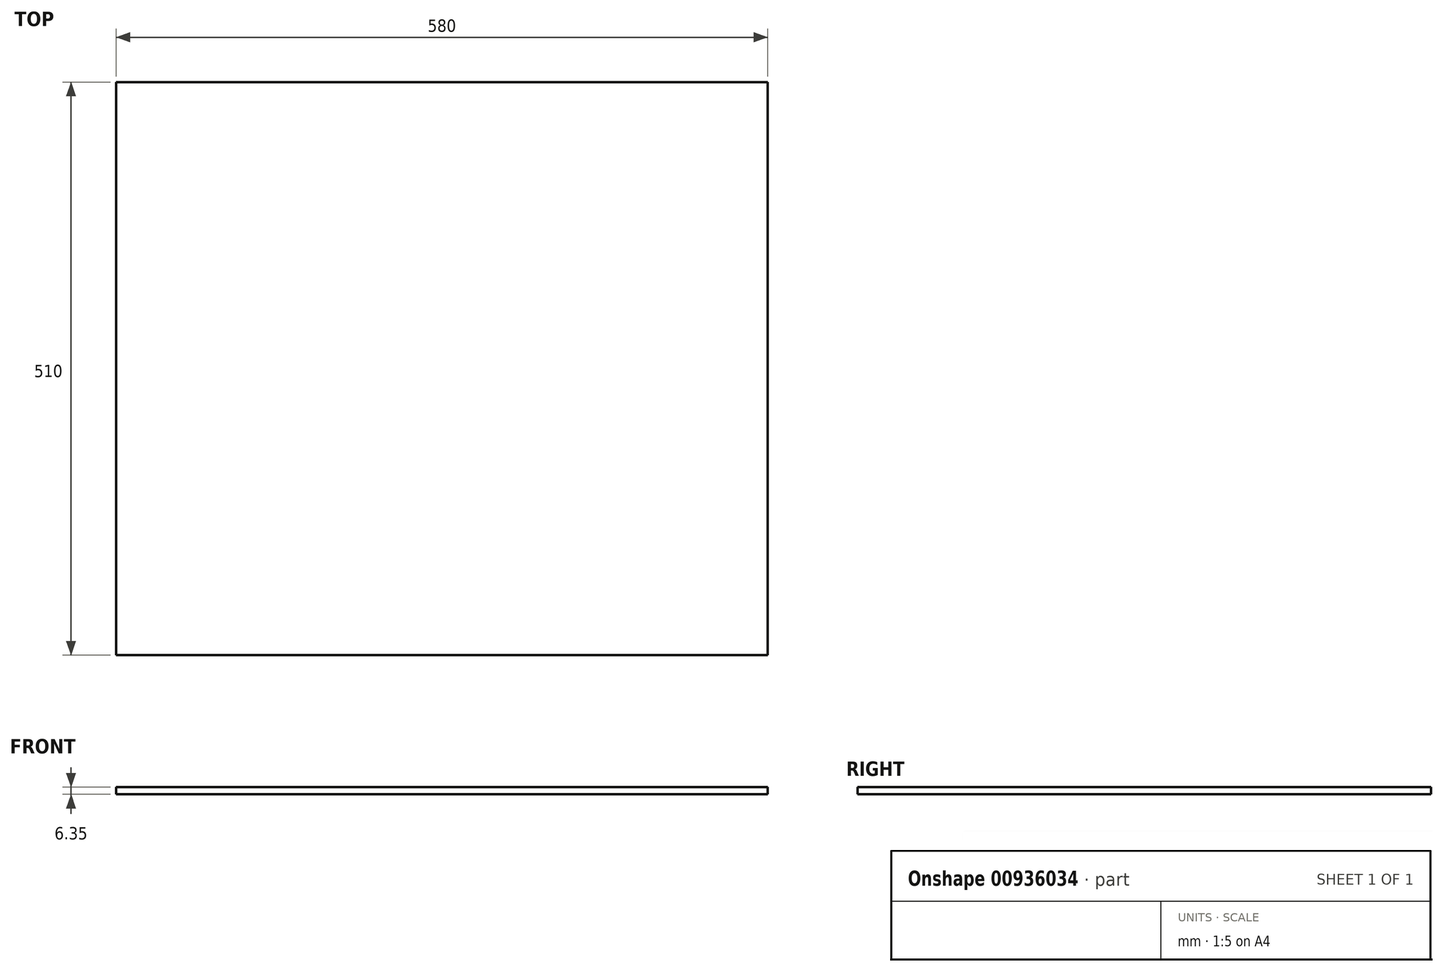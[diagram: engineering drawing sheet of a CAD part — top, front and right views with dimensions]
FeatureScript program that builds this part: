
annotation { "Feature Type Name" : "Feature", "Feature Type Description" : "" }
export const myFeature = defineFeature(function(context is Context, id is Id, definition is map)
    precondition{}
    {
        {
            var Q0;
            Q0=qCreatedBy(makeId("Top.planeOp"),FACE);
            var sketch = newSketch(context, id + "F0", { "sketchPlane" : qUnion([Q0])});
            skLineSegment(sketch, "E0.bottom", {"start": v(0, 0) * mm, "end": v(580, 0) * mm});
            skLineSegment(sketch, "E0.top", {"start": v(0, 510) * mm, "end": v(580, 510) * mm});
            skLineSegment(sketch, "E0.left", {"start": v(0, 0) * mm, "end": v(0, 510) * mm});
            skLineSegment(sketch, "E0.right", {"start": v(580, 0) * mm, "end": v(580, 510) * mm});
            skSolve(sketch);
        }
        {
            var Q0;
            Q0=makeQuery(id+"F0.imprint","IMPRINT",FACE,{"disambiguationData":[TD([[makeQuery(id+"F0.imprint","IMPRINT",EDGE,{"derivedFrom":sQuery(id+"F0.wireOp",EDGE,"E0.bottom")}),1.0]])]});
            extrude(context, id + "F1", {"entities" : qUnion([Q0]), "depth" : -6.35 * mm, "offsetDistance" : 25 * mm});
        }
    });
